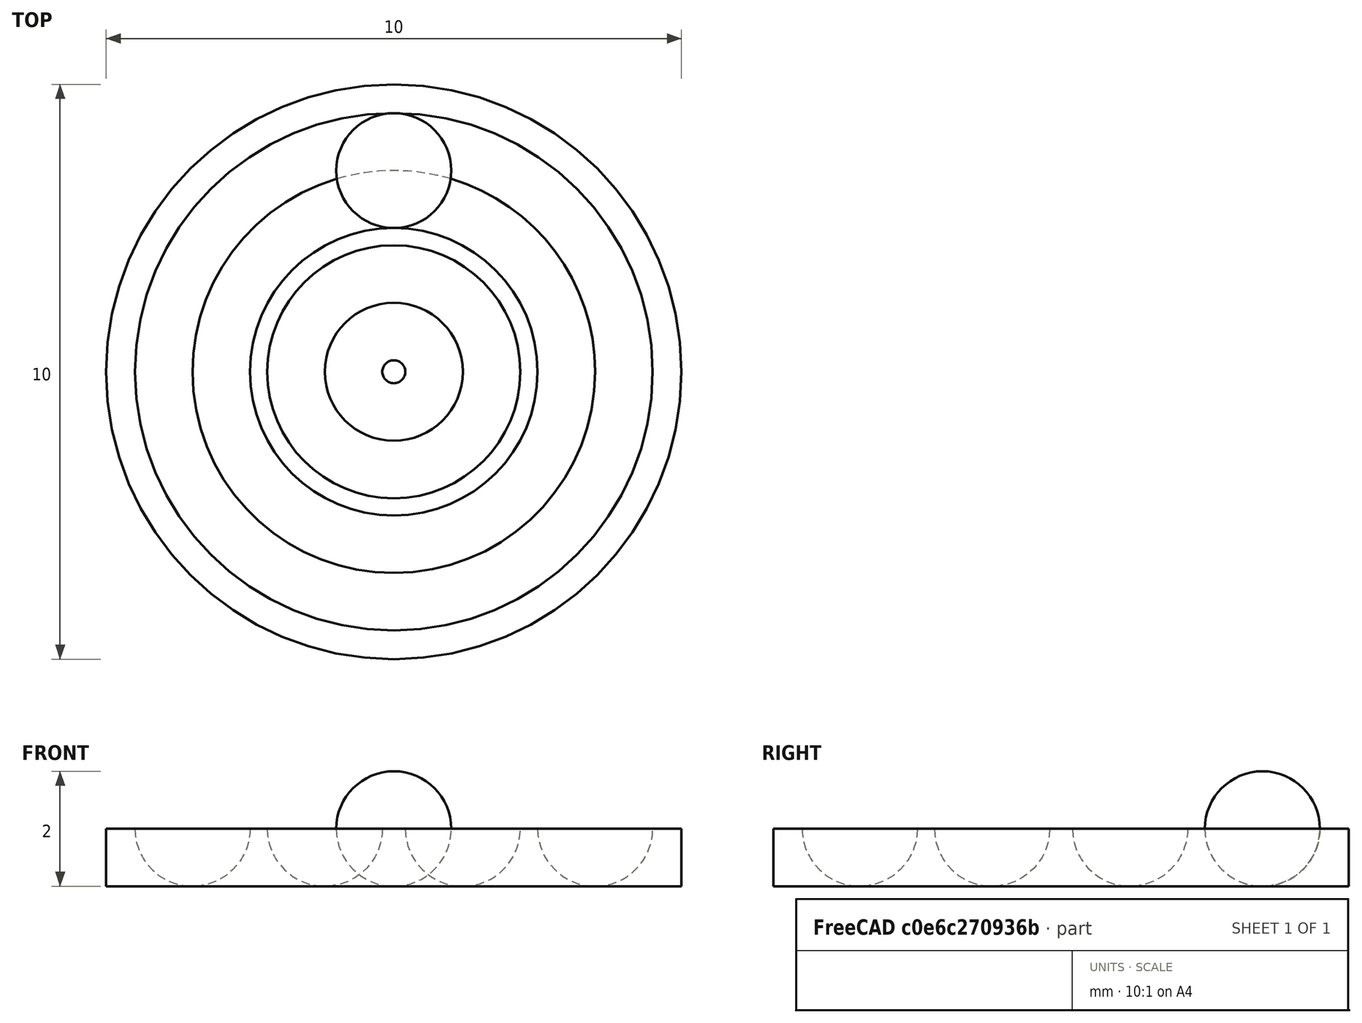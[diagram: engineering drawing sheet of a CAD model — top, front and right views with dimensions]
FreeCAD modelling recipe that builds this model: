
FCSTD DOCUMENT  (FreeCAD 0.20R29177 +426 (Git))
Label: juego
License: All rights reserved
LicenseURL: http://en.wikipedia.org/wiki/All_rights_reserved
objects: Part::Torus×2, Part::Cut×2, Part::Cylinder×1, Part::Sphere×1
note: 6 computed .brp shape members not serialized (recipe doc carries the construction recipe); baked Part::Feature solids carry a one-line shape summary decoded from their .brp

FEATURE [Part::Cylinder] Cylinder  label="Cilindro"
  Angle = 360
  AttacherType = Attacher::AttachEngine3D
  FirstAngle = 0
  Height = 1
  Radius = 5
  SecondAngle = 0
FEATURE [Part::Torus] Torus  label="Toro"
  Angle1 = -180
  Angle2 = 180
  Angle3 = 360
  AttacherType = Attacher::AttachEngine3D
  Placement = pos=(0,0,1) rot=(0,0,1;0rad)
  Radius1 = 3.5
  Radius2 = 1
FEATURE [Part::Cut] Cut
  Base = -> Cylinder
  Refine = true
  Tool = -> Torus
FEATURE [Part::Torus] Torus001  label="Toro001"
  Angle1 = -180
  Angle2 = 180
  Angle3 = 360
  AttacherType = Attacher::AttachEngine3D
  Placement = pos=(0,0,1) rot=(0,0,1;0rad)
  Radius1 = 1.2
  Radius2 = 1
FEATURE [Part::Cut] Cut001
  Base = -> Cut
  Refine = true
  Tool = -> Torus001
FEATURE [Part::Sphere] Sphere  label="Esfera"
  Angle1 = -90
  Angle2 = 90
  Angle3 = 360
  AttacherType = Attacher::AttachEngine3D
  Placement = pos=(0,3.5,1) rot=(0,0,1;0rad)
  Radius = 1
